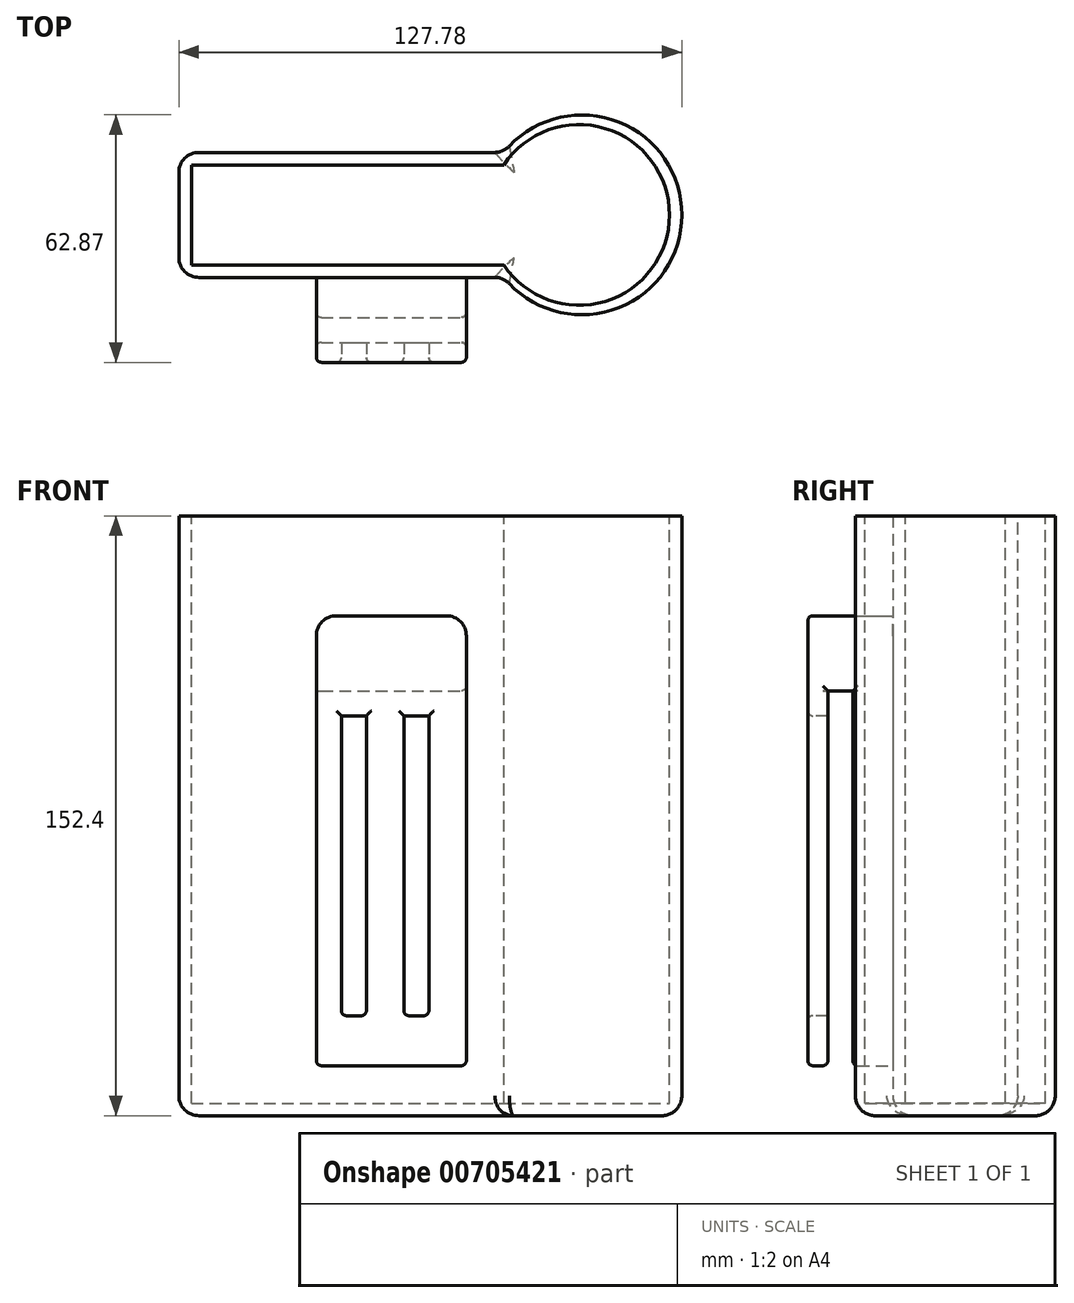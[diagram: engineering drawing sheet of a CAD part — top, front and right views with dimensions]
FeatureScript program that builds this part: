
annotation { "Feature Type Name" : "Feature", "Feature Type Description" : "" }
export const myFeature = defineFeature(function(context is Context, id is Id, definition is map)
    precondition{}
    {
        {
            var Q0;
            Q0=qCreatedBy(makeId("Top.planeOp"),FACE);
            var sketch = newSketch(context, id + "F0", { "sketchPlane" : qUnion([Q0])});
            skLineSegment(sketch, "E0.bottom", {"start": v(-76.2, 31.75) * mm, "end": v(6.35, 31.75) * mm});
            skLineSegment(sketch, "E0.top", {"start": v(-76.2, 0) * mm, "end": v(6.35, 0) * mm});
            skLineSegment(sketch, "E0.left", {"start": v(-76.2, 31.75) * mm, "end": v(-76.2, 0) * mm});
            skLineSegment(sketch, "E0.right", {"start": v(6.35, 31.75) * mm, "end": v(6.35, 0) * mm});
            skSolve(sketch);
        }
        {
            var Q0;
            Q0 = qSketchRegion(id + "F0", true);
            extrude(context, id + "F1", {"entities" : qUnion([Q0]), "depth" : 152.4 * mm, "offsetDistance" : 25.4 * mm});
        }
        {
            var Q0;
            Q0=makeQuery(id+"F1.opExtrude","CAP_FACE",FACE,{"disambiguationData":[OSD([sQuery(id+"F0.wireOp",EDGE,"E0.bottom"),sQuery(id+"F0.wireOp",EDGE,"E0.top"),sQuery(id+"F0.wireOp",EDGE,"E0.left"),sQuery(id+"F0.wireOp",EDGE,"E0.right")])],"isStart":false});
            var sketch = newSketch(context, id + "F2", { "sketchPlane" : qUnion([Q0])});
            skLineSegment(sketch, "E1.bottom", {"start": v(-73.03, 28.57) * mm, "end": v(6.35, 28.57) * mm});
            skLineSegment(sketch, "E1.top", {"start": v(-73.03, 3.17) * mm, "end": v(6.35, 3.17) * mm});
            skLineSegment(sketch, "E1.left", {"start": v(-73.03, 28.57) * mm, "end": v(-73.03, 3.17) * mm});
            skLineSegment(sketch, "E1.right", {"start": v(6.35, 28.57) * mm, "end": v(6.35, 3.17) * mm});
            skSolve(sketch);
        }
        {
            var Q0;
            Q0=makeQuery(id+"F2.imprint","IMPRINT",FACE,{"disambiguationData":[TD([[makeQuery(id+"F2.imprint","IMPRINT",EDGE,{"derivedFrom":sQuery(id+"F2.wireOp",EDGE,"E1.bottom")}),-1.0]])]});
            extrude(context, id + "F3", {"entities" : qUnion([Q0]), "operationType" : NewBodyOperationType.REMOVE, "oppositeDirection" : true, "depth" : 149.22 * mm, "offsetDistance" : 25.4 * mm});
        }
        {
            var Q0;
            Q0=makeQuery(id+"F1.opExtrude","CAP_FACE",FACE,{"disambiguationData":[OSD([sQuery(id+"F0.wireOp",EDGE,"E0.bottom"),sQuery(id+"F0.wireOp",EDGE,"E0.top"),sQuery(id+"F0.wireOp",EDGE,"E0.left"),sQuery(id+"F0.wireOp",EDGE,"E0.right")])],"isStart":true});
            var sketch = newSketch(context, id + "F4", { "sketchPlane" : qUnion([Q0])});
            skCircle(sketch, "E2", {"center": v(26.18, -15.88) * mm, "radius": 25.4 * mm});
            skPoint(sketch, "E2.first.point", {"position": v(6.35, 0) * mm});
            skPoint(sketch, "E2.second.point", {"position": v(6.35, -31.75) * mm});
            skPoint(sketch, "E2.third.point", {"position": v(51.58, -15.87) * mm});
            skPoint(sketch, "E2.third.point.positionSnap0", {"position": v(6.35, -15.88) * mm});
            skLineSegment(sketch, "E3", {"start": v(6.35, 0) * mm, "end": v(6.35, -31.75) * mm});
            skSolve(sketch);
        }
        {
            var Q0;
            {var subQ0=sQuery(id+"F4.wireOp",EDGE,"E3");Q0=makeQuery(id+"F4.imprint","IMPRINT",FACE,{"disambiguationData":[TD([[makeQuery(id+"F4.imprint","IMPRINT",EDGE,{"derivedFrom":subQ0}),-1.0]])]});}
            extrude(context, id + "F5", {"entities" : qUnion([Q0]), "operationType" : NewBodyOperationType.ADD, "oppositeDirection" : true, "depth" : 152.4 * mm, "offsetDistance" : 25.4 * mm});
        }
        {
            var Q0;
            Q0=makeQuery(id+"F5.boolean.opBoolean","MERGE",FACE,{"derivedFrom":[makeQuery(id+"F1.opExtrude","CAP_FACE",FACE,{"disambiguationData":[OSD([sQuery(id+"F0.wireOp",EDGE,"E0.bottom"),sQuery(id+"F0.wireOp",EDGE,"E0.top"),sQuery(id+"F0.wireOp",EDGE,"E0.left"),sQuery(id+"F0.wireOp",EDGE,"E0.right")])],"isStart":false}),makeQuery(id+"F5.opExtrude","CAP_FACE",FACE,{"disambiguationData":[OSD([sQuery(id+"F4.wireOp",EDGE,"E2"),sQuery(id+"F4.wireOp",EDGE,"E3")])],"isStart":false})]});
            var sketch = newSketch(context, id + "F6", { "sketchPlane" : qUnion([Q0])});
            skPoint(sketch, "E4.first.point", {"position": v(6.35, 28.57) * mm});
            skPoint(sketch, "E4.second.point", {"position": v(6.35, 3.17) * mm});
            skPoint(sketch, "E4.third.point", {"position": v(60.48, 15.88) * mm});
            skPoint(sketch, "E4.third.point.positionSnap0", {"position": v(51.58, 15.88) * mm});
            skCircle(sketch, "E5", {"center": v(25.47, 15.87) * mm, "radius": 22.95 * mm});
            skPoint(sketch, "E5.third.point", {"position": v(48.42, 15.88) * mm});
            skSolve(sketch);
        }
        {
            var Q0;
            {var subQ1=makeQuery(id+"F5.opExtrude","CAP_EDGE",EDGE,{"disambiguationData":[OSD([sQuery(id+"F4.wireOp",EDGE,"E3")])],"isStart":false});Q0=makeQuery(id+"F6.imprint","IMPRINT",FACE,{"disambiguationData":[TD([[makeQuery(id+"F6.imprint","IMPRINT",EDGE,{"derivedFrom":subQ1}),1.0]])]});}
            extrude(context, id + "F7", {"entities" : qUnion([Q0]), "operationType" : NewBodyOperationType.REMOVE, "oppositeDirection" : true, "depth" : 149.22 * mm, "offsetDistance" : 25.4 * mm});
        }
        {
            var Q0;
            Q0=makeQuery(id+"F1.opExtrude","SWEPT_FACE",FACE,{"disambiguationData":[OSD([sQuery(id+"F0.wireOp",EDGE,"E0.top")])]});
            var sketch = newSketch(context, id + "F8", { "sketchPlane" : qUnion([Q0])});
            skPoint(sketch, "E6.middle", {"position": v(0, 76.2) * mm});
            skPoint(sketch, "E6.middle.positionSnap0", {"position": v(6.35, 76.2) * mm});
            skPoint(sketch, "E6.centerSnap0", {"position": v(6.35, 76.2) * mm});
            skLineSegment(sketch, "E7.bottom", {"start": v(-41.27, 127) * mm, "end": v(-3.17, 127) * mm});
            skLineSegment(sketch, "E7.top", {"start": v(-41.27, 12.7) * mm, "end": v(-3.17, 12.7) * mm});
            skLineSegment(sketch, "E7.left", {"start": v(-41.27, 127) * mm, "end": v(-41.27, 12.7) * mm});
            skLineSegment(sketch, "E7.right", {"start": v(-3.17, 127) * mm, "end": v(-3.17, 12.7) * mm});
            skSolve(sketch);
        }
        {
            var Q0;
            Q0=makeQuery(id+"F8.imprint","IMPRINT",FACE,{"disambiguationData":[TD([[makeQuery(id+"F8.imprint","IMPRINT",EDGE,{"derivedFrom":sQuery(id+"F8.wireOp",EDGE,"E7.bottom")}),-1.0]])]});
            extrude(context, id + "F9", {"entities" : qUnion([Q0]), "operationType" : NewBodyOperationType.ADD, "depth" : 10.16 * mm, "offsetDistance" : 25.4 * mm});
        }
        {
            var Q0;
            Q0=makeQuery(id+"F9.opExtrude","CAP_FACE",FACE,{"disambiguationData":[OSD([sQuery(id+"F8.wireOp",EDGE,"E7.bottom"),sQuery(id+"F8.wireOp",EDGE,"E7.top"),sQuery(id+"F8.wireOp",EDGE,"E7.left"),sQuery(id+"F8.wireOp",EDGE,"E7.right")])],"isStart":false});
            var sketch = newSketch(context, id + "F10", { "sketchPlane" : qUnion([Q0])});
            skLineSegment(sketch, "E8.bottom", {"start": v(-41.27, 127) * mm, "end": v(-3.17, 127) * mm});
            skLineSegment(sketch, "E8.top", {"start": v(-41.27, 107.95) * mm, "end": v(-3.17, 107.95) * mm});
            skLineSegment(sketch, "E8.left", {"start": v(-41.27, 127) * mm, "end": v(-41.27, 107.95) * mm});
            skLineSegment(sketch, "E8.right", {"start": v(-3.17, 127) * mm, "end": v(-3.17, 107.95) * mm});
            skPoint(sketch, "E9.firstSnap0", {"position": v(-41.27, 117.47) * mm});
            skSolve(sketch);
        }
        {
            var Q0;
            Q0=makeQuery(id+"F10.imprint","IMPRINT",FACE,{"disambiguationData":[TD([[makeQuery(id+"F10.imprint","IMPRINT",EDGE,{"derivedFrom":sQuery(id+"F10.wireOp",EDGE,"E8.bottom")}),-1.0]])]});
            extrude(context, id + "F11", {"entities" : qUnion([Q0]), "operationType" : NewBodyOperationType.ADD, "depth" : 6.35 * mm, "offsetDistance" : 25.4 * mm});
        }
        {
            var Q0;
            Q0=makeQuery(id+"F11.opExtrude","CAP_FACE",FACE,{"disambiguationData":[OSD([sQuery(id+"F10.wireOp",EDGE,"E8.bottom"),sQuery(id+"F10.wireOp",EDGE,"E8.top"),sQuery(id+"F10.wireOp",EDGE,"E8.left"),sQuery(id+"F10.wireOp",EDGE,"E8.right")])],"isStart":false});
            var sketch = newSketch(context, id + "F12", { "sketchPlane" : qUnion([Q0])});
            skLineSegment(sketch, "E10.bottom", {"start": v(-41.27, 127) * mm, "end": v(-3.17, 127) * mm});
            skLineSegment(sketch, "E10.top", {"start": v(-41.27, 12.7) * mm, "end": v(-3.17, 12.7) * mm});
            skLineSegment(sketch, "E10.left", {"start": v(-41.27, 127) * mm, "end": v(-41.27, 12.7) * mm});
            skLineSegment(sketch, "E10.right", {"start": v(-3.17, 127) * mm, "end": v(-3.17, 12.7) * mm});
            skSolve(sketch);
        }
        {
            var Q0;
            {var subQ0=sQuery(id+"F12.wireOp",EDGE,"E10.top");Q0=makeQuery(id+"F12.imprint","IMPRINT",FACE,{"disambiguationData":[TD([[makeQuery(id+"F12.imprint","IMPRINT",EDGE,{"derivedFrom":subQ0}),1.0]])]});}
            var Q1;
            {var subQ0=sQuery(id+"F12.wireOp",EDGE,"E10.bottom");Q1=makeQuery(id+"F12.imprint","IMPRINT",FACE,{"disambiguationData":[TD([[makeQuery(id+"F12.imprint","IMPRINT",EDGE,{"derivedFrom":subQ0}),-1.0]])]});}
            extrude(context, id + "F13", {"entities" : qUnion([Q0, Q1]), "operationType" : NewBodyOperationType.ADD, "depth" : 5.08 * mm, "offsetDistance" : 25.4 * mm});
        }
        {
            var Q0;
            Q0=makeQuery(id+"F13.opExtrude","CAP_FACE",FACE,{"disambiguationData":[OSD([sQuery(id+"F12.wireOp",EDGE,"E10.bottom"),sQuery(id+"F12.wireOp",EDGE,"E10.top"),sQuery(id+"F12.wireOp",EDGE,"E10.left"),sQuery(id+"F12.wireOp",EDGE,"E10.right")])],"isStart":false});
            var sketch = newSketch(context, id + "F14", { "sketchPlane" : qUnion([Q0])});
            skLineSegment(sketch, "E11.bottom", {"start": v(-34.92, 101.6) * mm, "end": v(-28.57, 101.6) * mm});
            skLineSegment(sketch, "E11.top", {"start": v(-34.92, 25.4) * mm, "end": v(-28.57, 25.4) * mm});
            skLineSegment(sketch, "E11.left", {"start": v(-34.92, 101.6) * mm, "end": v(-34.92, 25.4) * mm});
            skLineSegment(sketch, "E11.right", {"start": v(-28.57, 101.6) * mm, "end": v(-28.57, 25.4) * mm});
            skLineSegment(sketch, "E12.bottom", {"start": v(-19.05, 101.6) * mm, "end": v(-12.7, 101.6) * mm});
            skLineSegment(sketch, "E12.top", {"start": v(-19.05, 25.4) * mm, "end": v(-12.7, 25.4) * mm});
            skLineSegment(sketch, "E12.left", {"start": v(-19.05, 101.6) * mm, "end": v(-19.05, 25.4) * mm});
            skLineSegment(sketch, "E12.right", {"start": v(-12.7, 101.6) * mm, "end": v(-12.7, 25.4) * mm});
            skSolve(sketch);
        }
        {
            var Q0;
            Q0=makeQuery(id+"F14.imprint","IMPRINT",FACE,{"disambiguationData":[TD([[makeQuery(id+"F14.imprint","IMPRINT",EDGE,{"derivedFrom":sQuery(id+"F14.wireOp",EDGE,"E12.bottom")}),-1.0]])]});
            var Q1;
            Q1=makeQuery(id+"F14.imprint","IMPRINT",FACE,{"disambiguationData":[TD([[makeQuery(id+"F14.imprint","IMPRINT",EDGE,{"derivedFrom":sQuery(id+"F14.wireOp",EDGE,"E11.bottom")}),-1.0]])]});
            extrude(context, id + "F15", {"entities" : qUnion([Q0, Q1]), "operationType" : NewBodyOperationType.REMOVE, "oppositeDirection" : true, "depth" : 5.08 * mm, "offsetDistance" : 25.4 * mm});
        }
        {
            var Q0;
            Q0=makeQuery(id+"F1.opExtrude","CAP_EDGE",EDGE,{"disambiguationData":[OSD([sQuery(id+"F0.wireOp",EDGE,"E0.top")])],"isStart":true});
            var Q1;
            Q1=makeQuery(id+"F5.opExtrude","CAP_EDGE",EDGE,{"disambiguationData":[OSD([sQuery(id+"F4.wireOp",EDGE,"E2")])],"isStart":true});
            var Q2;
            Q2=makeQuery(id+"F1.opExtrude","CAP_EDGE",EDGE,{"disambiguationData":[OSD([sQuery(id+"F0.wireOp",EDGE,"E0.bottom")])],"isStart":true});
            var Q3;
            Q3=makeQuery(id+"F5.boolean.opBoolean","MERGE",FACE,{"derivedFrom":[makeQuery(id+"F1.opExtrude","CAP_FACE",FACE,{"disambiguationData":[OSD([sQuery(id+"F0.wireOp",EDGE,"E0.bottom"),sQuery(id+"F0.wireOp",EDGE,"E0.top"),sQuery(id+"F0.wireOp",EDGE,"E0.left"),sQuery(id+"F0.wireOp",EDGE,"E0.right")])],"isStart":true}),makeQuery(id+"F5.opExtrude","CAP_FACE",FACE,{"disambiguationData":[OSD([sQuery(id+"F4.wireOp",EDGE,"E2"),sQuery(id+"F4.wireOp",EDGE,"E3")])],"isStart":true})]});
            fillet(context, id + "F16", {"entities" : qUnion([Q0, Q1, Q2, Q3]), "radius" : 5.08 * mm, "tangentPropagation" : true, "allowEdgeOverflow" : false});
        }
        {
            var Q0;
            Q0=makeQuery(id+"F1.opExtrude","SWEPT_EDGE",EDGE,{"disambiguationData":[OSD([sQuery(id+"F0.wireOp",EDGE,"E0.bottom"),sQuery(id+"F0.wireOp",EDGE,"E0.left")])]});
            var Q1;
            Q1=makeQuery(id+"F1.opExtrude","SWEPT_EDGE",EDGE,{"disambiguationData":[OSD([sQuery(id+"F0.wireOp",EDGE,"E0.top"),sQuery(id+"F0.wireOp",EDGE,"E0.left")])]});
            var Q2;
            {var subQ0=sQuery(id+"F0.wireOp",EDGE,"E0.top");Q2=makeQuery(id+"F5.boolean.opBoolean","MERGE",EDGE,{"derivedFrom":[makeQuery(id+"F1.opExtrude","SWEPT_EDGE",EDGE,{"disambiguationData":[OSD([subQ0,sQuery(id+"F0.wireOp",EDGE,"E0.right")])]}),makeQuery(id+"F5.opExtrude","SWEPT_EDGE",EDGE,{"disambiguationData":[OSD([subQ0,sQuery(id+"F4.wireOp",EDGE,"E2"),sQuery(id+"F4.wireOp",EDGE,"E3")])]})]});}
            var Q3;
            {var subQ0=sQuery(id+"F2.wireOp",EDGE,"E1.bottom");Q3=makeQuery(id+"F7.boolean.opBoolean","MERGE",EDGE,{"derivedFrom":[makeQuery(id+"F3.boolean.opBoolean","COPY",EDGE,{"derivedFrom":makeQuery(id+"F3.opExtrude","SWEPT_EDGE",EDGE,{"disambiguationData":[OSD([sQuery(id+"F0.wireOp",EDGE,"E0.right"),subQ0,sQuery(id+"F2.wireOp",EDGE,"E1.right")])]})}),makeQuery(id+"F7.opExtrude","SWEPT_EDGE",EDGE,{"disambiguationData":[OSD([subQ0,sQuery(id+"F4.wireOp",EDGE,"E3"),sQuery(id+"F6.wireOp",EDGE,"E4")])]})]});}
            var Q4;
            {var subQ0=sQuery(id+"F2.wireOp",EDGE,"E1.top");Q4=makeQuery(id+"F7.boolean.opBoolean","MERGE",EDGE,{"derivedFrom":[makeQuery(id+"F3.boolean.opBoolean","COPY",EDGE,{"derivedFrom":makeQuery(id+"F3.opExtrude","SWEPT_EDGE",EDGE,{"disambiguationData":[OSD([sQuery(id+"F0.wireOp",EDGE,"E0.right"),subQ0,sQuery(id+"F2.wireOp",EDGE,"E1.right")])]})}),makeQuery(id+"F7.opExtrude","SWEPT_EDGE",EDGE,{"disambiguationData":[OSD([subQ0,sQuery(id+"F4.wireOp",EDGE,"E3"),sQuery(id+"F6.wireOp",EDGE,"E4")])]})]});}
            var Q5;
            {var subQ0=sQuery(id+"F0.wireOp",EDGE,"E0.bottom");Q5=makeQuery(id+"F5.boolean.opBoolean","MERGE",EDGE,{"derivedFrom":[makeQuery(id+"F1.opExtrude","SWEPT_EDGE",EDGE,{"disambiguationData":[OSD([subQ0,sQuery(id+"F0.wireOp",EDGE,"E0.right")])]}),makeQuery(id+"F5.opExtrude","SWEPT_EDGE",EDGE,{"disambiguationData":[OSD([subQ0,sQuery(id+"F4.wireOp",EDGE,"E2"),sQuery(id+"F4.wireOp",EDGE,"E3")])]})]});}
            fillet(context, id + "F17", {"entities" : qUnion([Q0, Q1, Q2, Q3, Q4, Q5]), "radius" : 5.08 * mm, "tangentPropagation" : true, "allowEdgeOverflow" : false});
        }
        {
            var Q0;
            Q0=makeQuery(id+"F13.boolean.opBoolean","MERGE",EDGE,{"derivedFrom":[makeQuery(id+"F11.boolean.opBoolean","MERGE",EDGE,{"derivedFrom":[makeQuery(id+"F9.opExtrude","SWEPT_EDGE",EDGE,{"disambiguationData":[OSD([sQuery(id+"F8.wireOp",EDGE,"E7.bottom"),sQuery(id+"F8.wireOp",EDGE,"E7.left")])]}),makeQuery(id+"F11.opExtrude","SWEPT_EDGE",EDGE,{"disambiguationData":[OSD([sQuery(id+"F10.wireOp",EDGE,"E8.bottom"),sQuery(id+"F10.wireOp",EDGE,"E8.left")])]})]}),makeQuery(id+"F13.opExtrude","SWEPT_EDGE",EDGE,{"disambiguationData":[OSD([sQuery(id+"F12.wireOp",EDGE,"DnDNSQKr-Foka-8mTG-Lv2y-YWuiBGGa4El2.bottom"),sQuery(id+"F12.wireOp",EDGE,"DnDNSQKr-Foka-8mTG-Lv2y-YWuiBGGa4El2.left")])]})]});
            var Q1;
            Q1=makeQuery(id+"F13.boolean.opBoolean","MERGE",EDGE,{"derivedFrom":[makeQuery(id+"F11.boolean.opBoolean","MERGE",EDGE,{"derivedFrom":[makeQuery(id+"F9.opExtrude","SWEPT_EDGE",EDGE,{"disambiguationData":[OSD([sQuery(id+"F8.wireOp",EDGE,"E7.bottom"),sQuery(id+"F8.wireOp",EDGE,"E7.right")])]}),makeQuery(id+"F11.opExtrude","SWEPT_EDGE",EDGE,{"disambiguationData":[OSD([sQuery(id+"F10.wireOp",EDGE,"E8.bottom"),sQuery(id+"F10.wireOp",EDGE,"E8.right")])]})]}),makeQuery(id+"F13.opExtrude","SWEPT_EDGE",EDGE,{"disambiguationData":[OSD([sQuery(id+"F12.wireOp",EDGE,"DnDNSQKr-Foka-8mTG-Lv2y-YWuiBGGa4El2.bottom"),sQuery(id+"F12.wireOp",EDGE,"DnDNSQKr-Foka-8mTG-Lv2y-YWuiBGGa4El2.right")])]})]});
            var Q2;
            Q2=makeQuery(id+"F13.opExtrude","CAP_EDGE",EDGE,{"disambiguationData":[OSD([sQuery(id+"F12.wireOp",EDGE,"DnDNSQKr-Foka-8mTG-Lv2y-YWuiBGGa4El2.bottom")])],"isStart":false});
            var Q3;
            Q3=makeQuery(id+"F13.opExtrude","CAP_EDGE",EDGE,{"disambiguationData":[OSD([sQuery(id+"F12.wireOp",EDGE,"DnDNSQKr-Foka-8mTG-Lv2y-YWuiBGGa4El2.left")])],"isStart":false});
            var Q4;
            Q4=makeQuery(id+"F13.opExtrude","CAP_EDGE",EDGE,{"disambiguationData":[OSD([sQuery(id+"F12.wireOp",EDGE,"DnDNSQKr-Foka-8mTG-Lv2y-YWuiBGGa4El2.right")])],"isStart":false});
            var Q5;
            Q5=makeQuery(id+"F13.opExtrude","CAP_EDGE",EDGE,{"disambiguationData":[OSD([sQuery(id+"F12.wireOp",EDGE,"DnDNSQKr-Foka-8mTG-Lv2y-YWuiBGGa4El2.top")])],"isStart":false});
            var Q6;
            Q6=makeQuery(id+"F13.opExtrude","CAP_EDGE",EDGE,{"disambiguationData":[OSD([sQuery(id+"F12.wireOp",EDGE,"DnDNSQKr-Foka-8mTG-Lv2y-YWuiBGGa4El2.top")])],"isStart":true});
            var Q7;
            Q7=makeQuery(id+"F13.opExtrude","SWEPT_EDGE",EDGE,{"disambiguationData":[OSD([sQuery(id+"F12.wireOp",EDGE,"DnDNSQKr-Foka-8mTG-Lv2y-YWuiBGGa4El2.top"),sQuery(id+"F12.wireOp",EDGE,"DnDNSQKr-Foka-8mTG-Lv2y-YWuiBGGa4El2.left")])]});
            var Q8;
            Q8=makeQuery(id+"F13.opExtrude","SWEPT_EDGE",EDGE,{"disambiguationData":[OSD([sQuery(id+"F12.wireOp",EDGE,"DnDNSQKr-Foka-8mTG-Lv2y-YWuiBGGa4El2.top"),sQuery(id+"F12.wireOp",EDGE,"DnDNSQKr-Foka-8mTG-Lv2y-YWuiBGGa4El2.right")])]});
            fillet(context, id + "F18", {"entities" : qUnion([Q0, Q1, Q2, Q3, Q4, Q5, Q6, Q7, Q8]), "radius" : 5.08 * mm, "tangentPropagation" : true, "allowEdgeOverflow" : false});
        }
        {
            var Q0;
            Q0=makeQuery(id+"F15.boolean.opBoolean","COPY",EDGE,{"derivedFrom":makeQuery(id+"F15.opExtrude","CAP_EDGE",EDGE,{"disambiguationData":[OSD([sQuery(id+"F14.wireOp",EDGE,"E11.left")])],"isStart":true})});
            var Q1;
            Q1=makeQuery(id+"F15.boolean.opBoolean","COPY",EDGE,{"derivedFrom":makeQuery(id+"F15.opExtrude","CAP_EDGE",EDGE,{"disambiguationData":[OSD([sQuery(id+"F14.wireOp",EDGE,"E11.left")])],"isStart":false})});
            var Q2;
            Q2=makeQuery(id+"F15.boolean.opBoolean","COPY",EDGE,{"derivedFrom":makeQuery(id+"F15.opExtrude","CAP_EDGE",EDGE,{"disambiguationData":[OSD([sQuery(id+"F14.wireOp",EDGE,"E11.bottom")])],"isStart":true})});
            var Q3;
            Q3=makeQuery(id+"F15.boolean.opBoolean","COPY",EDGE,{"derivedFrom":makeQuery(id+"F15.opExtrude","CAP_EDGE",EDGE,{"disambiguationData":[OSD([sQuery(id+"F14.wireOp",EDGE,"E11.right")])],"isStart":true})});
            var Q4;
            Q4=makeQuery(id+"F13.opExtrude","CAP_FACE",FACE,{"disambiguationData":[OSD([sQuery(id+"F12.wireOp",EDGE,"E10.bottom"),sQuery(id+"F12.wireOp",EDGE,"E10.top"),sQuery(id+"F12.wireOp",EDGE,"E10.left"),sQuery(id+"F12.wireOp",EDGE,"E10.right")])],"isStart":false});
            var Q5;
            Q5=makeQuery(id+"F15.boolean.opBoolean","COPY",EDGE,{"derivedFrom":makeQuery(id+"F15.opExtrude","CAP_EDGE",EDGE,{"disambiguationData":[OSD([sQuery(id+"F14.wireOp",EDGE,"E12.left")])],"isStart":false})});
            var Q6;
            Q6=makeQuery(id+"F15.boolean.opBoolean","COPY",EDGE,{"derivedFrom":makeQuery(id+"F15.opExtrude","CAP_EDGE",EDGE,{"disambiguationData":[OSD([sQuery(id+"F14.wireOp",EDGE,"E12.top")])],"isStart":false})});
            var Q7;
            Q7=makeQuery(id+"F15.boolean.opBoolean","COPY",EDGE,{"derivedFrom":makeQuery(id+"F15.opExtrude","SWEPT_EDGE",EDGE,{"disambiguationData":[OSD([sQuery(id+"F14.wireOp",EDGE,"E11.top"),sQuery(id+"F14.wireOp",EDGE,"E11.left")])]})});
            var Q8;
            Q8=makeQuery(id+"F15.boolean.opBoolean","COPY",EDGE,{"derivedFrom":makeQuery(id+"F15.opExtrude","SWEPT_EDGE",EDGE,{"disambiguationData":[OSD([sQuery(id+"F14.wireOp",EDGE,"E12.top"),sQuery(id+"F14.wireOp",EDGE,"E12.left")])]})});
            var Q9;
            Q9=makeQuery(id+"F15.boolean.opBoolean","COPY",EDGE,{"derivedFrom":makeQuery(id+"F15.opExtrude","CAP_EDGE",EDGE,{"disambiguationData":[OSD([sQuery(id+"F14.wireOp",EDGE,"E11.top")])],"isStart":false})});
            var Q10;
            Q10=makeQuery(id+"F13.opExtrude","CAP_EDGE",EDGE,{"disambiguationData":[OSD([sQuery(id+"F12.wireOp",EDGE,"E10.right")])],"isStart":true});
            var Q11;
            Q11=makeQuery(id+"F11.opExtrude","SWEPT_EDGE",EDGE,{"disambiguationData":[OSD([sQuery(id+"F8.wireOp",EDGE,"E7.right"),sQuery(id+"F10.wireOp",EDGE,"E8.top"),sQuery(id+"F10.wireOp",EDGE,"E8.right")])]});
            var Q12;
            Q12=makeQuery(id+"F9.opExtrude","CAP_EDGE",EDGE,{"disambiguationData":[OSD([sQuery(id+"F8.wireOp",EDGE,"E7.right")])],"isStart":false});
            var Q13;
            Q13=makeQuery(id+"F9.opExtrude","CAP_EDGE",EDGE,{"disambiguationData":[OSD([sQuery(id+"F8.wireOp",EDGE,"E7.top")])],"isStart":false});
            var Q14;
            Q14=makeQuery(id+"F13.opExtrude","SWEPT_EDGE",EDGE,{"disambiguationData":[OSD([sQuery(id+"F12.wireOp",EDGE,"E10.top"),sQuery(id+"F12.wireOp",EDGE,"E10.right")])]});
            var Q15;
            Q15=makeQuery(id+"F15.boolean.opBoolean","COPY",EDGE,{"derivedFrom":makeQuery(id+"F15.opExtrude","SWEPT_EDGE",EDGE,{"disambiguationData":[OSD([sQuery(id+"F14.wireOp",EDGE,"E11.top"),sQuery(id+"F14.wireOp",EDGE,"E11.right")])]})});
            var Q16;
            Q16=makeQuery(id+"F15.boolean.opBoolean","COPY",EDGE,{"derivedFrom":makeQuery(id+"F15.opExtrude","SWEPT_EDGE",EDGE,{"disambiguationData":[OSD([sQuery(id+"F14.wireOp",EDGE,"E12.top"),sQuery(id+"F14.wireOp",EDGE,"E12.right")])]})});
            var Q17;
            Q17=makeQuery(id+"F15.boolean.opBoolean","COPY",EDGE,{"derivedFrom":makeQuery(id+"F15.opExtrude","CAP_EDGE",EDGE,{"disambiguationData":[OSD([sQuery(id+"F14.wireOp",EDGE,"E11.right")])],"isStart":false})});
            var Q18;
            Q18=makeQuery(id+"F15.boolean.opBoolean","COPY",EDGE,{"derivedFrom":makeQuery(id+"F15.opExtrude","CAP_EDGE",EDGE,{"disambiguationData":[OSD([sQuery(id+"F14.wireOp",EDGE,"E12.right")])],"isStart":false})});
            fillet(context, id + "F19", {"entities" : qUnion([Q0, Q1, Q2, Q3, Q4, Q5, Q6, Q7, Q8, Q9, Q10, Q11, Q12, Q13, Q14, Q15, Q16, Q17, Q18]), "radius" : 1.27 * mm, "tangentPropagation" : true, "allowEdgeOverflow" : false});
        }
        {
            var Q0;
            Q0=makeQuery(id+"F13.opExtrude","CAP_EDGE",EDGE,{"disambiguationData":[OSD([sQuery(id+"F12.wireOp",EDGE,"E10.left")])],"isStart":true});
            var Q1;
            Q1=makeQuery(id+"F13.opExtrude","SWEPT_EDGE",EDGE,{"disambiguationData":[OSD([sQuery(id+"F12.wireOp",EDGE,"E10.top"),sQuery(id+"F12.wireOp",EDGE,"E10.left")])]});
            var Q2;
            Q2=makeQuery(id+"F13.opExtrude","CAP_EDGE",EDGE,{"disambiguationData":[OSD([sQuery(id+"F12.wireOp",EDGE,"E10.top")])],"isStart":true});
            var Q3;
            Q3=makeQuery(id+"F9.opExtrude","CAP_EDGE",EDGE,{"disambiguationData":[OSD([sQuery(id+"F8.wireOp",EDGE,"E7.left")])],"isStart":false});
            var Q4;
            Q4=makeQuery(id+"F11.opExtrude","CAP_EDGE",EDGE,{"disambiguationData":[OSD([sQuery(id+"F10.wireOp",EDGE,"E8.top")])],"isStart":true});
            var Q5;
            Q5=makeQuery(id+"F15.boolean.opBoolean","COPY",EDGE,{"derivedFrom":makeQuery(id+"F15.opExtrude","CAP_EDGE",EDGE,{"disambiguationData":[OSD([sQuery(id+"F14.wireOp",EDGE,"E12.bottom")])],"isStart":false})});
            var Q6;
            Q6=makeQuery(id+"F15.boolean.opBoolean","COPY",EDGE,{"derivedFrom":makeQuery(id+"F15.opExtrude","CAP_EDGE",EDGE,{"disambiguationData":[OSD([sQuery(id+"F14.wireOp",EDGE,"E11.bottom")])],"isStart":false})});
            var Q7;
            Q7=makeQuery(id+"F9.opExtrude","SWEPT_EDGE",EDGE,{"disambiguationData":[OSD([sQuery(id+"F8.wireOp",EDGE,"E7.top"),sQuery(id+"F8.wireOp",EDGE,"E7.right")])]});
            fillet(context, id + "F20", {"entities" : qUnion([Q0, Q1, Q2, Q3, Q4, Q5, Q6, Q7]), "radius" : 1.27 * mm, "tangentPropagation" : true, "allowEdgeOverflow" : false});
        }
    });
